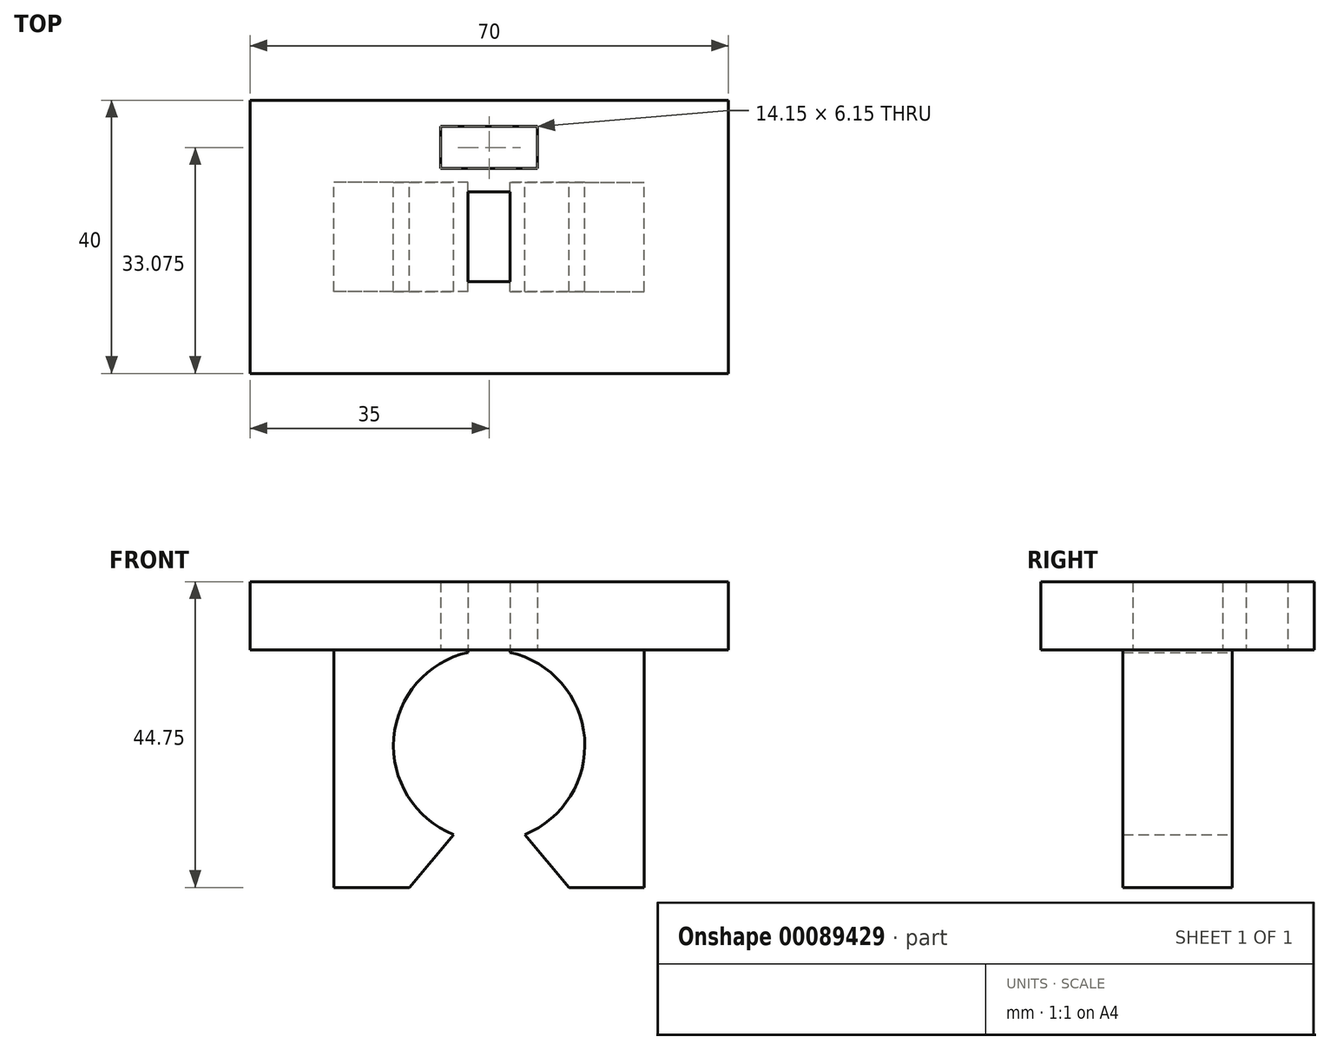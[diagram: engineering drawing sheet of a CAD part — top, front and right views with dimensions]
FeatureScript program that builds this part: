
annotation { "Feature Type Name" : "Feature", "Feature Type Description" : "" }
export const myFeature = defineFeature(function(context is Context, id is Id, definition is map)
    precondition{}
    {
        {
            var Q0;
            Q0=qCreatedBy(makeId("Top.planeOp"),FACE);
            var sketch = newSketch(context, id + "F0", { "sketchPlane" : qUnion([Q0])});
            skLineSegment(sketch, "E0.bottom", {"start": v(35, 20) * mm, "end": v(-35, 20) * mm});
            skLineSegment(sketch, "E0.top", {"start": v(35, -20) * mm, "end": v(-35, -20) * mm});
            skLineSegment(sketch, "E0.left", {"start": v(35, 20) * mm, "end": v(35, -20) * mm});
            skLineSegment(sketch, "E0.right", {"start": v(-35, 20) * mm, "end": v(-35, -20) * mm});
            skPoint(sketch, "E0.middle", {"position": v(0, 0) * mm});
            skLineSegment(sketch, "E1.bottom", {"start": v(3.08, 6.57) * mm, "end": v(-3.07, 6.57) * mm});
            skLineSegment(sketch, "E1.top", {"start": v(3.07, -6.58) * mm, "end": v(-3.08, -6.58) * mm});
            skLineSegment(sketch, "E1.left", {"start": v(3.08, 6.57) * mm, "end": v(3.07, -6.58) * mm});
            skLineSegment(sketch, "E1.right", {"start": v(-3.07, 6.57) * mm, "end": v(-3.08, -6.58) * mm});
            skLineSegment(sketch, "E2.bottom", {"start": v(7.07, 10) * mm, "end": v(-7.08, 10) * mm});
            skLineSegment(sketch, "E2.top", {"start": v(7.07, 16.15) * mm, "end": v(-7.08, 16.15) * mm});
            skLineSegment(sketch, "E2.left", {"start": v(7.07, 10) * mm, "end": v(7.07, 16.15) * mm});
            skLineSegment(sketch, "E2.right", {"start": v(-7.08, 10) * mm, "end": v(-7.08, 16.15) * mm});
            skPoint(sketch, "E2.middle", {"position": v(0, 13.07) * mm});
            skSolve(sketch);
        }
        {
            var Q0;
            Q0=makeQuery(id+"F0.imprint","IMPRINT",FACE,{"disambiguationData":[TD([[makeQuery(id+"F0.imprint","IMPRINT",EDGE,{"derivedFrom":sQuery(id+"F0.wireOp",EDGE,"E0.bottom")}),1.0]])]});
            extrude(context, id + "F1", {"entities" : qUnion([Q0]), "depth" : 10 * mm});
        }
        {
            var Q0;
            Q0=qCreatedBy(makeId("Front.planeOp"),FACE);
            var sketch = newSketch(context, id + "F2", { "sketchPlane" : qUnion([Q0])});
            skLineSegment(sketch, "E3", {"start": v(-22.7, 0) * mm, "end": v(-22.7, -34.75) * mm});
            skLineSegment(sketch, "E4", {"start": v(-5.2, -27) * mm, "end": v(-11.7, -34.75) * mm});
            skLineSegment(sketch, "E5", {"start": v(-11.7, -34.75) * mm, "end": v(-22.7, -34.75) * mm});
            skArc(sketch, "E6", {"start": v(-3.08, -0.34) * mm, "mid": v(-13.96, -12.89) * mm, "end": v(-5.2, -27) * mm});
            skLineSegment(sketch, "E7", {"start": v(-3.08, -0.34) * mm, "end": v(-3.08, 0) * mm});
            skLineSegment(sketch, "E8", {"start": v(-3.08, 0) * mm, "end": v(3.08, 0) * mm, "construction": true});
            skPoint(sketch, "E9.orphan", {"position": v(0, 0) * mm});
            skLineSegment(sketch, "E10", {"start": v(-3.07, 0) * mm, "end": v(-22.7, 0) * mm});
            skArc(sketch, "E11.MirrorCS", {"start": v(3.08, -0.34) * mm, "mid": v(13.96, -12.89) * mm, "end": v(5.2, -27) * mm});
            skLineSegment(sketch, "E12.MirrorCS", {"start": v(3.08, -0.34) * mm, "end": v(3.08, 0) * mm});
            skLineSegment(sketch, "E13.MirrorCS", {"start": v(3.07, 0) * mm, "end": v(22.7, 0) * mm});
            skLineSegment(sketch, "E14.MirrorCS", {"start": v(22.7, 0) * mm, "end": v(22.7, -34.75) * mm});
            skLineSegment(sketch, "E15.MirrorCS", {"start": v(5.2, -27) * mm, "end": v(11.7, -34.75) * mm});
            skLineSegment(sketch, "E16.MirrorCS", {"start": v(11.7, -34.75) * mm, "end": v(22.7, -34.75) * mm});
            skSolve(sketch);
        }
        {
            var Q0;
            Q0 = qSketchRegion(id + "F2", true);
            extrude(context, id + "F3", {"entities" : qUnion([Q0]), "operationType" : NewBodyOperationType.ADD, "endBound" : BoundingType.SYMMETRIC, "depth" : 16 * mm});
        }
    });
